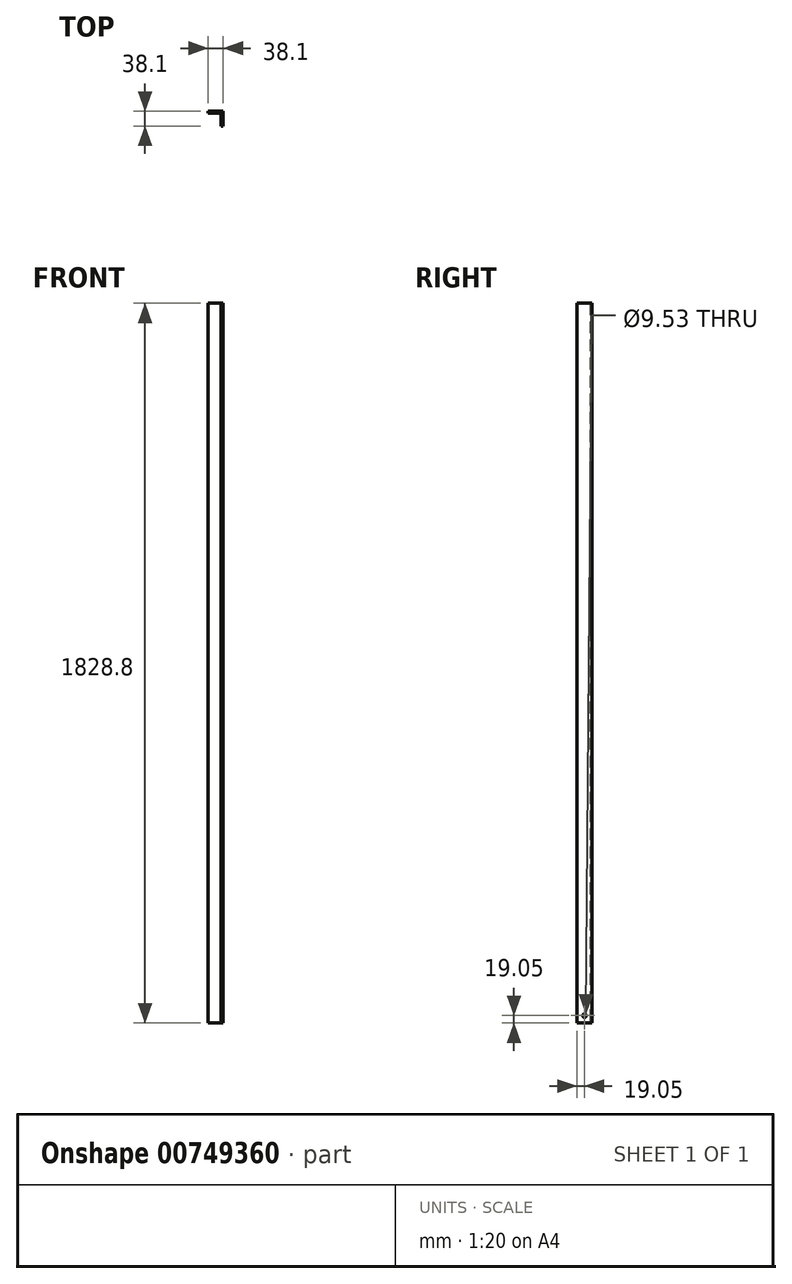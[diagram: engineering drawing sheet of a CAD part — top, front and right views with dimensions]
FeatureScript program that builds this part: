
annotation { "Feature Type Name" : "Feature", "Feature Type Description" : "" }
export const myFeature = defineFeature(function(context is Context, id is Id, definition is map)
    precondition{}
    {
        {
            var Q0;
            Q0=qCreatedBy(makeId("Top.planeOp"),FACE);
            var sketch = newSketch(context, id + "F0", { "sketchPlane" : qUnion([Q0])});
            skLineSegment(sketch, "E0", {"start": v(0, 0) * mm, "end": v(38.1, 0) * mm});
            skLineSegment(sketch, "E1", {"start": v(38.1, 0) * mm, "end": v(38.1, -38.1) * mm});
            skLineSegment(sketch, "E2", {"start": v(38.1, -38.1) * mm, "end": v(33.34, -38.1) * mm});
            skLineSegment(sketch, "E3", {"start": v(33.34, -38.1) * mm, "end": v(33.34, -4.76) * mm});
            skLineSegment(sketch, "E4", {"start": v(33.34, -4.76) * mm, "end": v(0, -4.76) * mm});
            skLineSegment(sketch, "E5", {"start": v(0, -4.76) * mm, "end": v(0, 0) * mm});
            skSolve(sketch);
        }
        {
            var Q0;
            Q0=makeQuery(id+"F0.imprint","IMPRINT",FACE,{"disambiguationData":[TD([[makeQuery(id+"F0.imprint","IMPRINT",EDGE,{"derivedFrom":sQuery(id+"F0.wireOp",EDGE,"E0")}),-1.0]])]});
            extrude(context, id + "F1", {"entities" : qUnion([Q0]), "depth" : 1828.8 * mm, "offsetDistance" : 25.4 * mm});
        }
        {
            var Q0;
            Q0=makeQuery(id+"F1.opExtrude","SWEPT_FACE",FACE,{"disambiguationData":[OSD([sQuery(id+"F0.wireOp",EDGE,"E1")])]});
            var sketch = newSketch(context, id + "F2", { "sketchPlane" : qUnion([Q0])});
            skCircle(sketch, "E6", {"center": v(-19.05, 19.05) * mm, "radius": 4.76 * mm});
            skSolve(sketch);
        }
        {
            var Q0;
            Q0=makeQuery(id+"F2.imprint","IMPRINT",FACE,{"disambiguationData":[TD([[makeQuery(id+"F2.imprint","IMPRINT",EDGE,{"derivedFrom":sQuery(id+"F2.wireOp",EDGE,"E6")}),1.0]])]});
            extrude(context, id + "F3", {"entities" : qUnion([Q0]), "operationType" : NewBodyOperationType.REMOVE, "endBound" : BoundingType.THROUGH_ALL, "oppositeDirection" : true, "depth" : 25.4 * mm, "offsetDistance" : 25.4 * mm});
        }
    });
